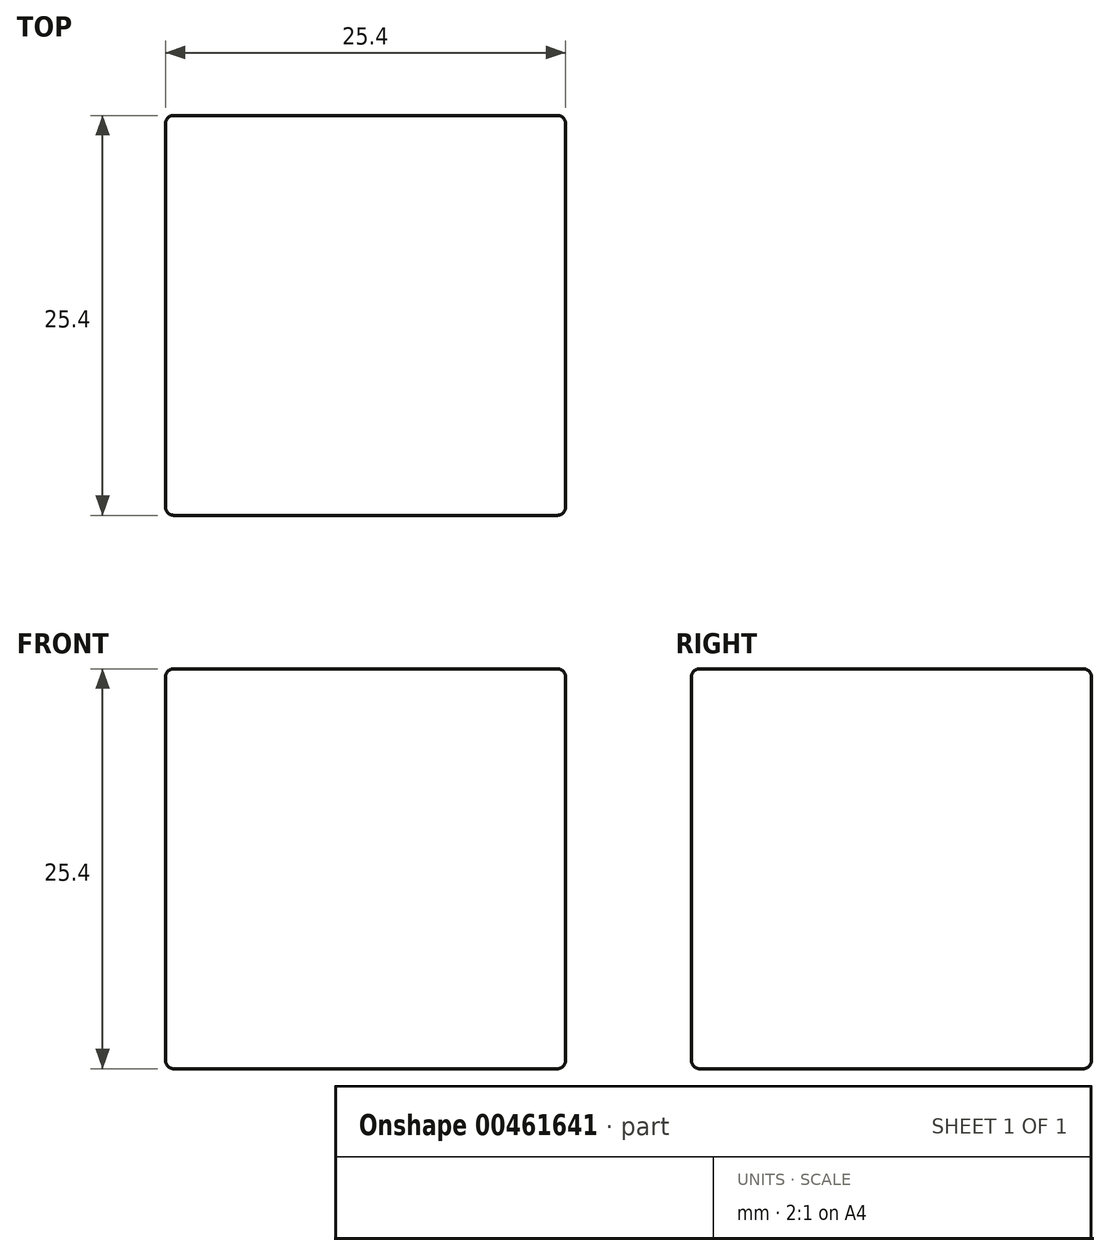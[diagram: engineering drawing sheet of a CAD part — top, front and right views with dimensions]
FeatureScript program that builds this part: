
annotation { "Feature Type Name" : "Feature", "Feature Type Description" : "" }
export const myFeature = defineFeature(function(context is Context, id is Id, definition is map)
    precondition{}
    {
        {
            var Q0;
            Q0=qCreatedBy(makeId("Top.planeOp"),FACE);
            var sketch = newSketch(context, id + "F0", { "sketchPlane" : qUnion([Q0])});
            skLineSegment(sketch, "E0.rect.bottom", {"start": v(12.7, 12.7) * mm, "end": v(-12.7, 12.7) * mm});
            skLineSegment(sketch, "E0.rect.top", {"start": v(12.7, -12.7) * mm, "end": v(-12.7, -12.7) * mm});
            skLineSegment(sketch, "E0.rect.left", {"start": v(12.7, 12.7) * mm, "end": v(12.7, -12.7) * mm});
            skLineSegment(sketch, "E0.rect.right", {"start": v(-12.7, 12.7) * mm, "end": v(-12.7, -12.7) * mm});
            skPoint(sketch, "E0.rect.middle", {"position": v(0, 0) * mm});
            skSolve(sketch);
        }
        {
            var Q0;
            Q0=qSketchRegion(id+"F0",true);
            extrude(context, id + "F1", {"entities" : qUnion([Q0]), "depth" : 25.4 * mm});
        }
        {
            var Q0;
            Q0=makeQuery(id+"F1.opExtrude","SWEPT_FACE",FACE,{"disambiguationData":[OSD([sQuery(id+"F0.wireOp",EDGE,"E0.rect.bottom")])]});
            var Q1;
            Q1=makeQuery(id+"F1.opExtrude","SWEPT_FACE",FACE,{"disambiguationData":[OSD([sQuery(id+"F0.wireOp",EDGE,"E0.rect.top")])]});
            var Q2;
            Q2=makeQuery(id+"F1.opExtrude","CAP_FACE",FACE,{"disambiguationData":[OSD([sQuery(id+"F0.wireOp",EDGE,"E0.rect.bottom"),sQuery(id+"F0.wireOp",EDGE,"E0.rect.top"),sQuery(id+"F0.wireOp",EDGE,"E0.rect.left"),sQuery(id+"F0.wireOp",EDGE,"E0.rect.right")])],"isStart":true});
            var Q3;
            Q3=makeQuery(id+"F1.opExtrude","CAP_FACE",FACE,{"disambiguationData":[OSD([sQuery(id+"F0.wireOp",EDGE,"E0.rect.bottom"),sQuery(id+"F0.wireOp",EDGE,"E0.rect.top"),sQuery(id+"F0.wireOp",EDGE,"E0.rect.left"),sQuery(id+"F0.wireOp",EDGE,"E0.rect.right")])],"isStart":false});
            fillet(context, id + "F2", {"entities" : qUnion([Q0, Q1, Q2, Q3]), "radius" : 0.5 * mm, "tangentPropagation" : true, "allowEdgeOverflow" : false});
        }
    });
